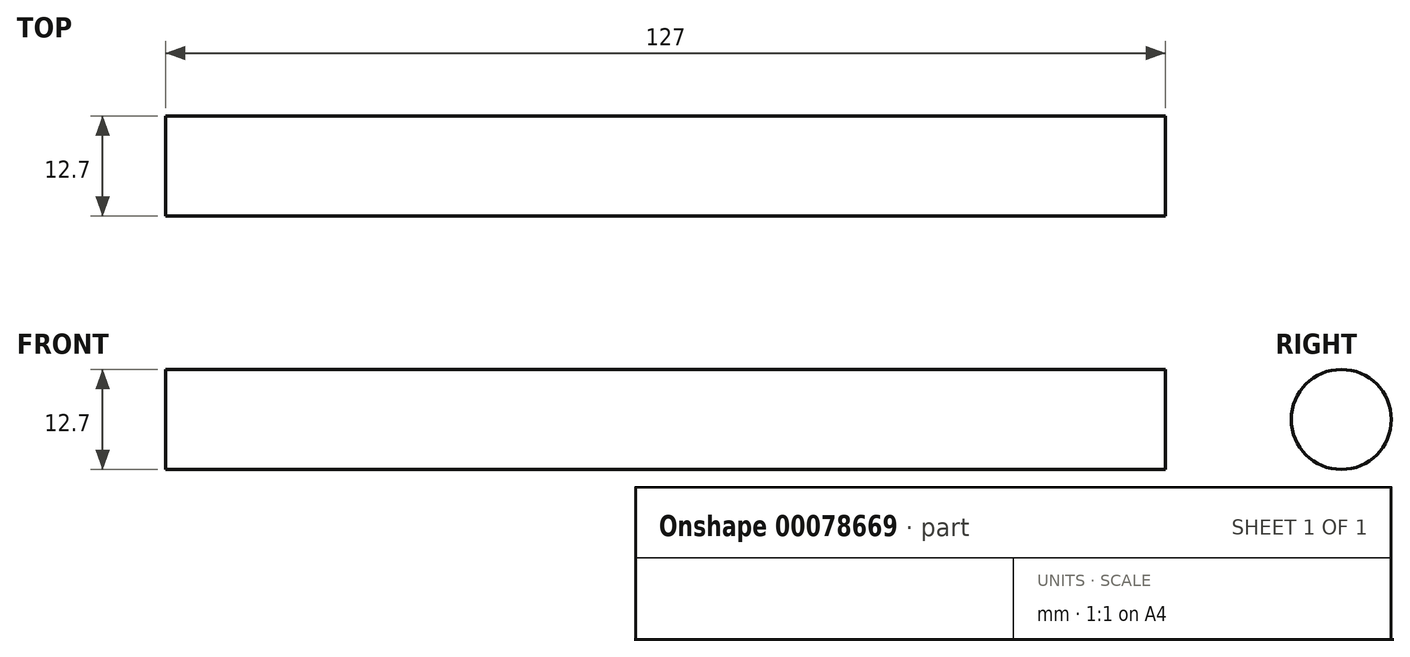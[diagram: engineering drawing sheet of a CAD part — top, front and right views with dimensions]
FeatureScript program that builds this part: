
annotation { "Feature Type Name" : "Feature", "Feature Type Description" : "" }
export const myFeature = defineFeature(function(context is Context, id is Id, definition is map)
    precondition{}
    {
        {
            var Q0;
            Q0=qCreatedBy(makeId("Right.planeOp"),FACE);
            var sketch = newSketch(context, id + "F0", { "sketchPlane" : qUnion([Q0])});
            skCircle(sketch, "E0", {"center": v(-54.13, 31.24) * mm, "radius": 6.35 * mm});
            skSolve(sketch);
        }
        {
            var Q0;
            Q0 = qSketchRegion(id + "F0", true);
            extrude(context, id + "F1", {"entities" : qUnion([Q0]), "depth" : 127 * mm});
        }
    });
